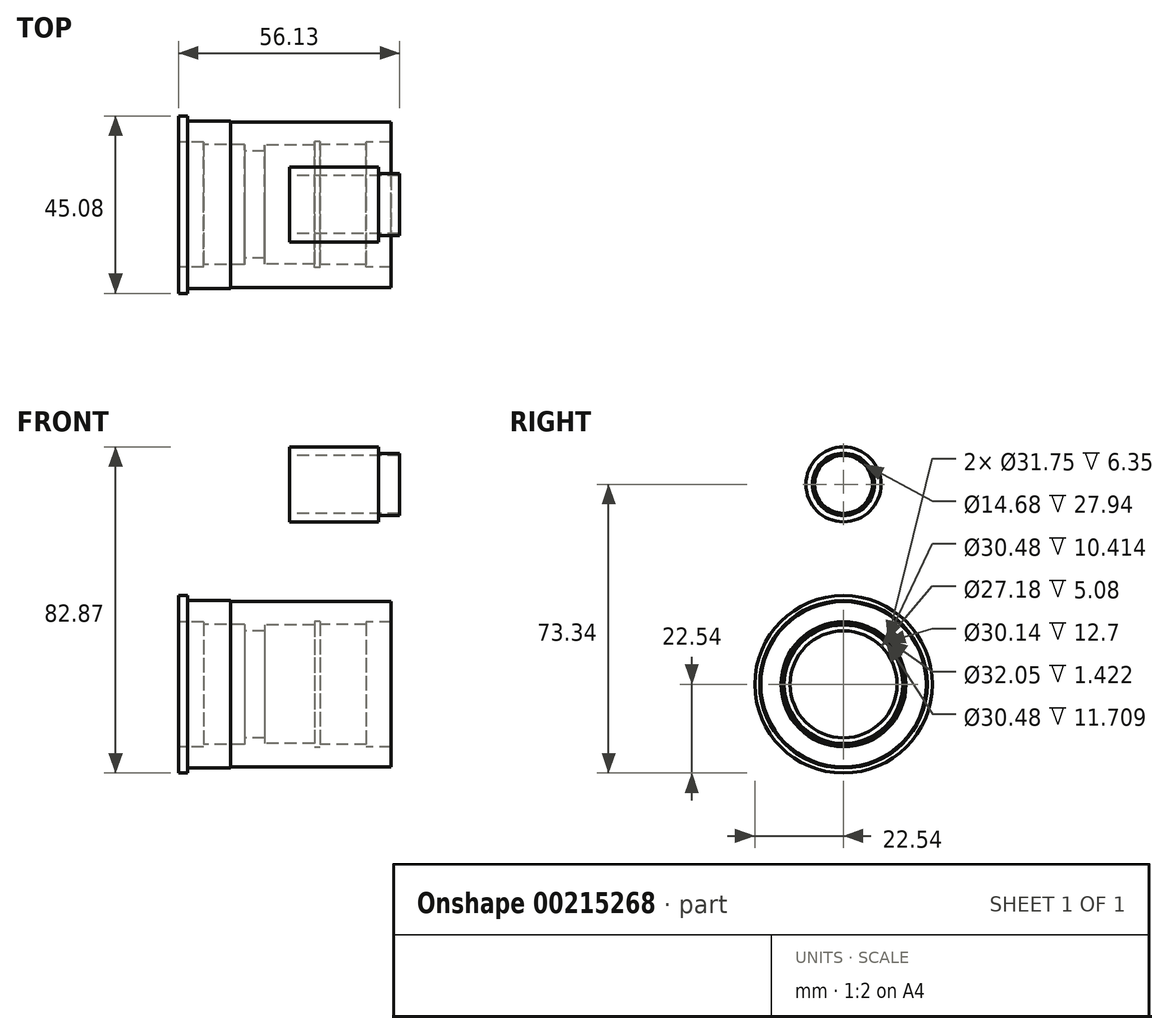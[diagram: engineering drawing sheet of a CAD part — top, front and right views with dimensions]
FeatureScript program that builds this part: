
annotation { "Feature Type Name" : "Feature", "Feature Type Description" : "" }
export const myFeature = defineFeature(function(context is Context, id is Id, definition is map)
    precondition{}
    {
        {
            var Q0;
            Q0=qCreatedBy(makeId("Top.planeOp"),FACE);
            var sketch = newSketch(context, id + "F0", { "sketchPlane" : qUnion([Q0])});
            skLineSegment(sketch, "E0", {"start": v(-62.98, 0) * mm, "end": v(67.82, 0) * mm, "construction": true});
            skLineSegment(sketch, "E1", {"start": v(-6.35, 15.07) * mm, "end": v(6.35, 15.07) * mm});
            skLineSegment(sketch, "E2", {"start": v(-6.35, 13.59) * mm, "end": v(-11.43, 13.59) * mm});
            skLineSegment(sketch, "E3", {"start": v(-11.43, 15.24) * mm, "end": v(-21.84, 15.24) * mm});
            skLineSegment(sketch, "E4", {"start": v(-28.2, 15.88) * mm, "end": v(-21.84, 15.88) * mm});
            skLineSegment(sketch, "E5", {"start": v(6.35, 15.07) * mm, "end": v(6.35, 16.03) * mm});
            skLineSegment(sketch, "E6", {"start": v(6.35, 16.03) * mm, "end": v(7.77, 16.03) * mm});
            skLineSegment(sketch, "E7", {"start": v(7.77, 16.03) * mm, "end": v(7.77, 15.24) * mm});
            skLineSegment(sketch, "E8", {"start": v(7.77, 15.24) * mm, "end": v(19.48, 15.24) * mm});
            skLineSegment(sketch, "E9", {"start": v(19.48, 15.24) * mm, "end": v(19.48, 15.88) * mm});
            skLineSegment(sketch, "E10", {"start": v(19.48, 15.88) * mm, "end": v(25.83, 15.88) * mm});
            skLineSegment(sketch, "E11", {"start": v(-11.43, 15.24) * mm, "end": v(-11.43, 13.59) * mm});
            skLineSegment(sketch, "E12", {"start": v(-21.84, 15.88) * mm, "end": v(-21.84, 15.24) * mm});
            skLineSegment(sketch, "E13", {"start": v(-6.35, 15.07) * mm, "end": v(-6.35, 13.59) * mm});
            skLineSegment(sketch, "E14", {"start": v(-28.2, 15.88) * mm, "end": v(-28.2, 22.54) * mm});
            skLineSegment(sketch, "E15", {"start": v(-28.2, 22.54) * mm, "end": v(-25.9, 22.54) * mm});
            skLineSegment(sketch, "E16", {"start": v(-25.9, 22.54) * mm, "end": v(-25.9, 21.27) * mm});
            skLineSegment(sketch, "E17", {"start": v(-25.9, 21.27) * mm, "end": v(-14.99, 21.27) * mm});
            skLineSegment(sketch, "E18", {"start": v(-14.99, 21.27) * mm, "end": v(-14.99, 21.02) * mm});
            skLineSegment(sketch, "E19", {"start": v(-14.99, 21.02) * mm, "end": v(25.83, 21.02) * mm});
            skLineSegment(sketch, "E20", {"start": v(25.83, 21.02) * mm, "end": v(25.83, 15.88) * mm});
            skSolve(sketch);
        }
        {
            var Q0;
            Q0=makeQuery(id+"F0.imprint","IMPRINT",FACE,{"disambiguationData":[TD([[makeQuery(id+"F0.imprint","IMPRINT",EDGE,{"derivedFrom":sQuery(id+"F0.wireOp",EDGE,"E1")}),1.0]])]});
            var Q1;
            Q1=sQuery(id+"F0.wireOp",EDGE,"E0");
            revolve(context, id + "F1", {"surfaceOperationType" : NewSurfaceOperationType.NEW, "entities" : qUnion([Q0]), "axis" : qUnion([Q1]), "revolveType" : RevolveType.FULL});
        }
        {
            var Q0;
            Q0=qCreatedBy(makeId("Top.planeOp"),FACE);
            cPlane(context, id + "F2", {"entities" : qUnion([Q0]), "cplaneType" : CPlaneType.OFFSET, "offset" : 50.8 * mm, "width" : 152.4 * mm, "height" : 152.4 * mm});
        }
        {
            var Q0;
            Q0=qCreatedBy(id+"F2.planeOp",FACE);
            var sketch = newSketch(context, id + "F3", { "sketchPlane" : qUnion([Q0])});
            skPoint(sketch, "E21.0", {"position": v(0, 0) * mm});
            skLineSegment(sketch, "E22", {"start": v(-105.37, 0) * mm, "end": v(104.6, 0) * mm, "construction": true});
            skLineSegment(sketch, "E23", {"start": v(0, 7.34) * mm, "end": v(27.94, 7.34) * mm});
            skLineSegment(sketch, "E24", {"start": v(0, 7.34) * mm, "end": v(0, 9.53) * mm});
            skLineSegment(sketch, "E25", {"start": v(0, 9.53) * mm, "end": v(22.54, 9.53) * mm});
            skLineSegment(sketch, "E26", {"start": v(22.54, 9.53) * mm, "end": v(22.54, 7.9) * mm});
            skLineSegment(sketch, "E27", {"start": v(22.54, 7.9) * mm, "end": v(27.94, 7.9) * mm});
            skLineSegment(sketch, "E28", {"start": v(27.94, 7.9) * mm, "end": v(27.94, 7.34) * mm});
            skSolve(sketch);
        }
        {
            var Q0;
            Q0=makeQuery(id+"F3.imprint","IMPRINT",FACE,{"disambiguationData":[TD([[makeQuery(id+"F3.imprint","IMPRINT",EDGE,{"derivedFrom":sQuery(id+"F3.wireOp",EDGE,"E23")}),1.0]])]});
            var Q1;
            Q1=sQuery(id+"F3.wireOp",EDGE,"E22");
            revolve(context, id + "F4", {"surfaceOperationType" : NewSurfaceOperationType.NEW, "entities" : qUnion([Q0]), "axis" : qUnion([Q1]), "revolveType" : RevolveType.FULL});
        }
    });
